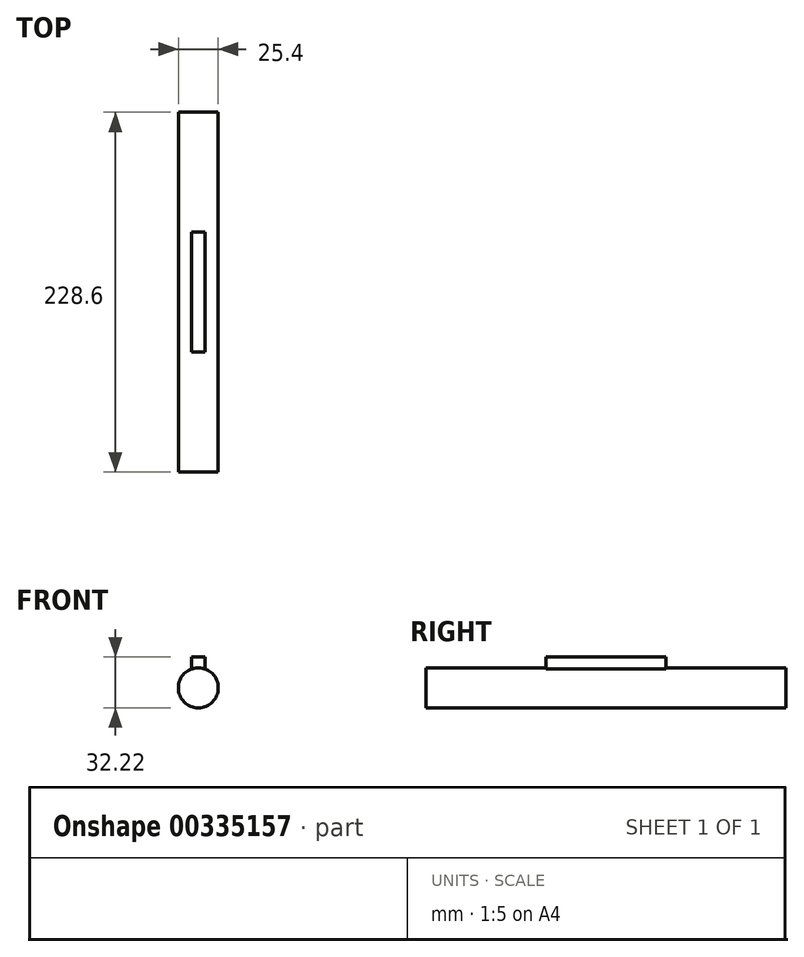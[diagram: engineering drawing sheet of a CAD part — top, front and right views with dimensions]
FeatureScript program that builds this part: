
annotation { "Feature Type Name" : "Feature", "Feature Type Description" : "" }
export const myFeature = defineFeature(function(context is Context, id is Id, definition is map)
    precondition{}
    {
        {
            var Q0;
            Q0=qCreatedBy(makeId("Front.planeOp"),FACE);
            var sketch = newSketch(context, id + "F0", { "sketchPlane" : qUnion([Q0])});
            skCircle(sketch, "E0", {"center": v(0, 0) * mm, "radius": 12.7 * mm});
            skLineSegment(sketch, "E1", {"start": v(-4.44, 11.9) * mm, "end": v(-4.45, 19.52) * mm});
            skLineSegment(sketch, "E2.MirrorCS", {"start": v(4.45, 11.9) * mm, "end": v(4.45, 19.52) * mm});
            skLineSegment(sketch, "E3", {"start": v(4.44, 19.52) * mm, "end": v(-4.44, 19.52) * mm});
            skSolve(sketch);
        }
        {
            var Q0;
            Q0 = qSketchRegion(id + "F0", true);
            extrude(context, id + "F1", {"entities" : qUnion([Q0]), "depth" : 76.2 * mm, "offsetDistance" : 25.4 * mm});
        }
        {
            var Q0;
            {var subQ0=sQuery(id+"F0.wireOp",EDGE,"E0");var subQ1=makeQuery(id+"F0.imprint","INTERSECT",VERTEX,{"derivedFrom":[subQ0,sQuery(id+"F0.wireOp",EDGE,"E1")]});Q0=makeQuery(id+"F0.imprint","IMPRINT",FACE,{"disambiguationData":[TD([[makeQuery(id+"F0.imprint","IMPRINT",EDGE,{"disambiguationData":[TD([[subQ1,1.0]])],"derivedFrom":subQ0}),1.0]])]});}
            extrude(context, id + "F2", {"entities" : qUnion([Q0]), "operationType" : NewBodyOperationType.ADD, "oppositeDirection" : true, "depth" : 76.2 * mm, "offsetDistance" : 25.4 * mm, "hasSecondDirection" : true, "secondDirectionOppositeDirection" : false, "secondDirectionDepth" : 152.4 * mm});
        }
    });
